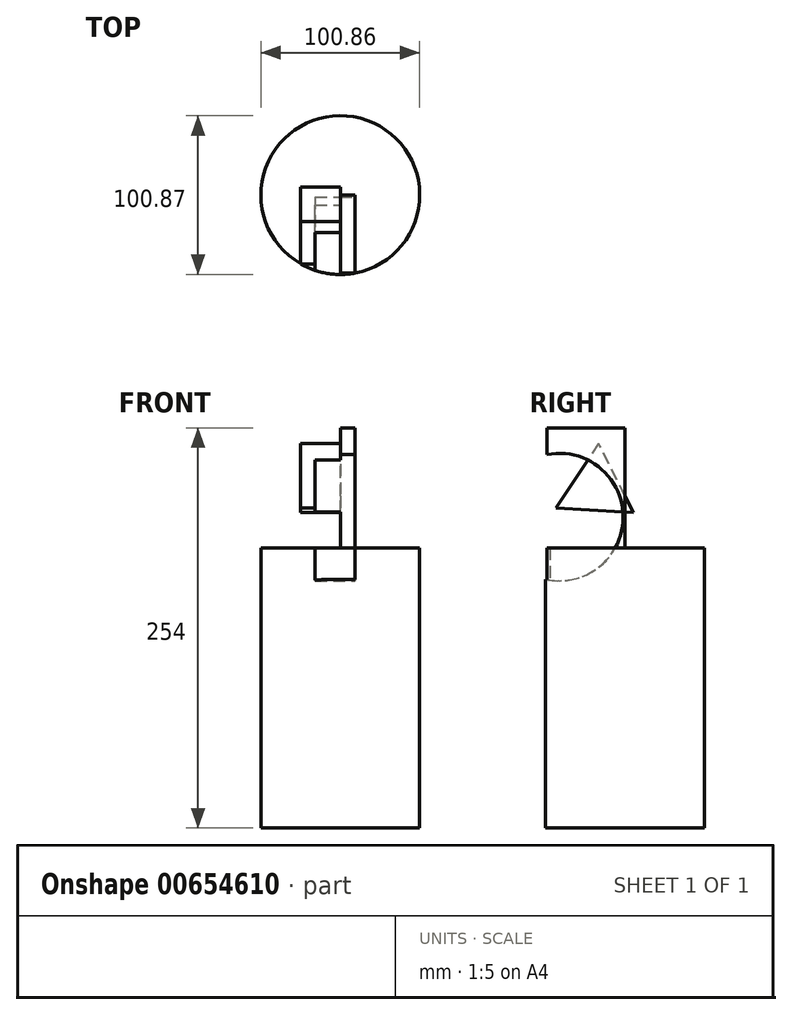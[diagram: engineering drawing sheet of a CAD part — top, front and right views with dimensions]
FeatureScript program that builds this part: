
annotation { "Feature Type Name" : "Feature", "Feature Type Description" : "" }
export const myFeature = defineFeature(function(context is Context, id is Id, definition is map)
    precondition{}
    {
        {
            var Q0;
            Q0=qCreatedBy(makeId("Top.planeOp"),FACE);
            var sketch = newSketch(context, id + "F0", { "sketchPlane" : qUnion([Q0])});
            skCircle(sketch, "E0", {"center": v(0, 0) * mm, "radius": 50.43 * mm});
            skSolve(sketch);
        }
        {
            var Q0;
            Q0=makeQuery(id+"F0.imprint","IMPRINT",FACE,{"disambiguationData":[TD([[makeQuery(id+"F0.imprint","IMPRINT",EDGE,{"derivedFrom":sQuery(id+"F0.wireOp",EDGE,"E0")}),1.0]])]});
            extrude(context, id + "F1", {"entities" : qUnion([Q0]), "depth" : 177.8 * mm, "offsetDistance" : 25.4 * mm});
        }
        {
            var Q0;
            Q0=makeQuery(id+"F1.opExtrude","CAP_FACE",FACE,{"disambiguationData":[OSD([sQuery(id+"F0.wireOp",EDGE,"E0")])],"isStart":false});
            var sketch = newSketch(context, id + "F2", { "sketchPlane" : qUnion([Q0])});
            skLineSegment(sketch, "E1.bottom", {"start": v(0, 0) * mm, "end": v(9.43, 0) * mm});
            skLineSegment(sketch, "E1.top", {"start": v(0, -49.54) * mm, "end": v(9.43, -49.54) * mm});
            skLineSegment(sketch, "E1.left", {"start": v(0, 0) * mm, "end": v(0, -49.54) * mm});
            skLineSegment(sketch, "E1.right", {"start": v(9.43, 0) * mm, "end": v(9.43, -49.54) * mm});
            skSolve(sketch);
        }
        {
            var Q0;
            Q0 = qSketchRegion(id + "F2", true);
            extrude(context, id + "F3", {"entities" : qUnion([Q0]), "operationType" : NewBodyOperationType.ADD, "depth" : 76.2 * mm, "offsetDistance" : 25.4 * mm});
        }
        {
            var Q0;
            Q0=makeQuery(id+"F3.opExtrude","SWEPT_FACE",FACE,{"disambiguationData":[OSD([sQuery(id+"F2.wireOp",EDGE,"E1.left")])]});
            var sketch = newSketch(context, id + "F4", { "sketchPlane" : qUnion([Q0])});
            skCircle(sketch, "E2.cCircle", {"center": v(18.46, 215.9) * mm, "radius": 14.17 * mm, "construction": true});
            skPoint(sketch, "E2.cCircle.centerSnap0", {"position": v(49.54, 215.9) * mm});
            skLineSegment(sketch, "E2.0", {"start": v(-5.22, 200.34) * mm, "end": v(16.82, 244.2) * mm});
            skLineSegment(sketch, "E2.1", {"start": v(16.82, 244.2) * mm, "end": v(43.78, 203.17) * mm});
            skLineSegment(sketch, "E2.2", {"start": v(43.78, 203.17) * mm, "end": v(-5.22, 200.34) * mm});
            skPoint(sketch, "E2.0.midPoint", {"position": v(5.8, 222.26) * mm});
            skSolve(sketch);
        }
        {
            var Q0;
            Q0 = qSketchRegion(id + "F4", true);
            extrude(context, id + "F5", {"entities" : qUnion([Q0]), "operationType" : NewBodyOperationType.ADD, "depth" : 25.4 * mm, "offsetDistance" : 25.4 * mm});
        }
        {
            var Q0;
            Q0=makeQuery(id+"F3.opExtrude","SWEPT_FACE",FACE,{"disambiguationData":[OSD([sQuery(id+"F2.wireOp",EDGE,"E1.right")])]});
            var sketch = newSketch(context, id + "F6", { "sketchPlane" : qUnion([Q0])});
            skCircle(sketch, "E3", {"center": v(-41.7, 197.41) * mm, "radius": 40.47 * mm});
            skSolve(sketch);
        }
        {
            var Q0;
            Q0 = qSketchRegion(id + "F6", true);
            extrude(context, id + "F7", {"entities" : qUnion([Q0]), "operationType" : NewBodyOperationType.REMOVE, "oppositeDirection" : true, "depth" : 25.4 * mm, "offsetDistance" : 25.4 * mm});
        }
    });
